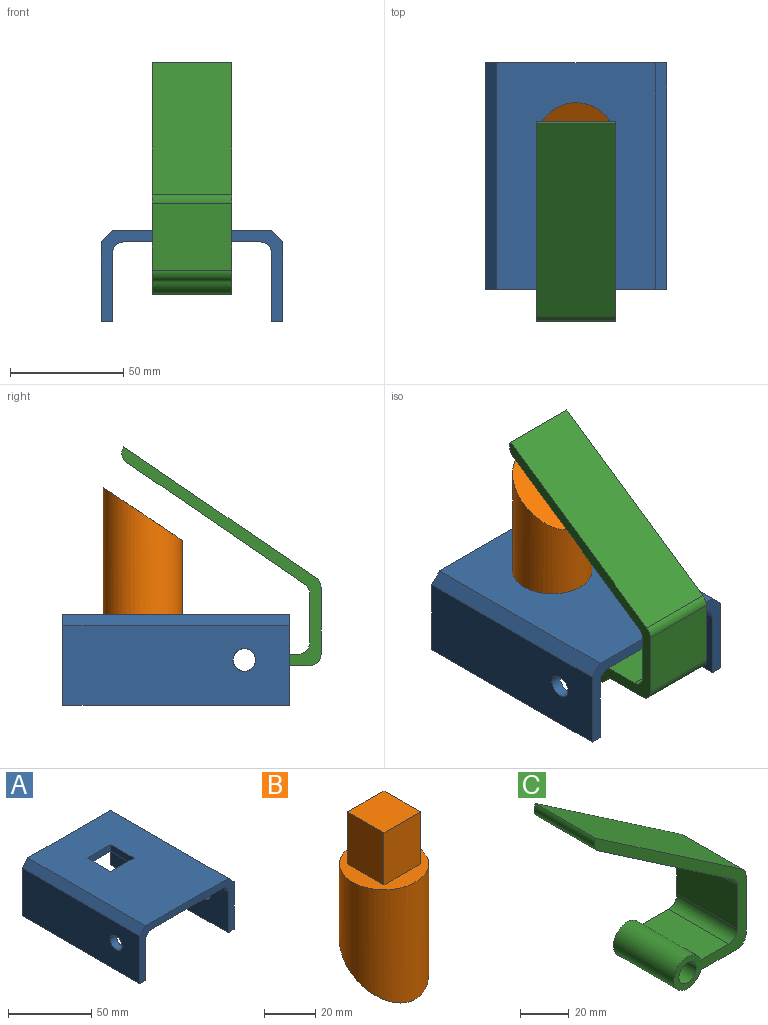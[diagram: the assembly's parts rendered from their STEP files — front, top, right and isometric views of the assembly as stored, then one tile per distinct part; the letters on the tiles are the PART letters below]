
ASSEMBLY  parts=3 mates=4
PART A: 20 faces, bbox 80x100x40 mm
  f0: plane 100x70mm, normal (0,0,1), area 6600mm2, adj f10,f11,f12,f13,f14,f15,f16,f17
  f1: plane 100x60mm, normal (0,0,-1), area 5600mm2, adj f2,f9,f10,f11,f14,f15,f16,f17
  f2: cylinder r=5mm len=100mm, axis (0,1,0), area 785.4mm2, adj f1,f3,f10,f11
  f3: plane 100x30mm, normal (-1,0,0), area 2921.5mm2, adj f2,f4,f10,f11,f19
  f4: plane 100x5mm, normal (0,0,-1), area 500mm2, adj f3,f5,f10,f11
  f5: plane 100x35mm, normal (1,0,0), area 3421.5mm2, adj f4,f10,f11,f13,f19
  f6: plane 100x35mm, normal (-1,0,0), area 3421.5mm2, adj f7,f10,f11,f12,f18
  f7: plane 100x5mm, normal (0,0,-1), area 500mm2, adj f6,f8,f10,f11
  f8: plane 100x30mm, normal (1,0,0), area 2921.5mm2, adj f7,f9,f10,f11,f18
  f9: cylinder r=5mm len=100mm, axis (0,1,0), area 785.4mm2, adj f1,f8,f10,f11
  f10: plane 80x40mm, normal (0,-1,0), area 735.7mm2, adj f0,f1,f2,f3,f4,f5,f6,f7
  f11: plane 80x40mm, normal (0,1,0), area 735.7mm2, adj f0,f1,f2,f3,f4,f5,f6,f7
  f12: plane 100x5mm, normal (-0.71,0,0.71), area 707.1mm2, adj f0,f6,f10,f11
  f13: plane 100x5mm, normal (0.71,0,0.71), area 707.1mm2, adj f0,f5,f10,f11
  f14: plane 20x5mm, normal (0,1,0), area 100mm2, adj f0,f1,f15,f17
  f15: plane 20x5mm, normal (-1,0,0), area 100mm2, adj f0,f1,f14,f16
  f16: plane 20x5mm, normal (0,-1,0), area 100mm2, adj f0,f1,f15,f17
  f17: plane 20x5mm, normal (1,0,0), area 100mm2, adj f0,f1,f14,f16
  f18: cylinder r=5mm len=10mm, axis (1,0,0), area 157.1mm2, adj f6,f8
  f19: cylinder r=5mm len=10mm, axis (1,0,0), area 157.1mm2, adj f3,f5
PART B: 8 faces, bbox 39.9x39.9x86.1 mm
  f0: cylinder r=17.5mm len=56.2mm, axis (0,0,1), area 4930.3mm2, adj f1,f7
  f1: plane 35x35mm, normal (0,0,1), area 562.1mm2, adj f0,f2,f3,f4,f5
  f2: plane 25x20mm, normal (1,0,0), area 500mm2, adj f1,f3,f5,f6
  f3: plane 25x20mm, normal (0,1,0), area 500mm2, adj f1,f2,f4,f6
  f4: plane 25x20mm, normal (-1,0,0), area 500mm2, adj f1,f3,f5,f6
  f5: plane 25x20mm, normal (0,-1,0), area 500mm2, adj f1,f2,f4,f6
  f6: plane 20x20mm, normal (0,0,1), area 400mm2, adj f2,f3,f4,f5
  f7: plane 39.92x39.92mm, normal (0,0.56,-0.83), area 1157.4mm2, adj f0
PART C: 15 faces, bbox 87.9x35x102.1 mm
  f0: plane 84.81x57.97mm, normal (0.56,0,0.83), area 3595.5mm2, adj f1,f12,f13,f14
  f1: cylinder r=5mm len=35mm, axis (0,-1,0), area 274.9mm2, adj f0,f2,f13,f14
  f2: plane 78.5x53.66mm, normal (-0.56,0,-0.83), area 3328.2mm2, adj f1,f3,f13,f14
  f3: cylinder r=5mm len=35mm, axis (0,-1,0), area 170mm2, adj f2,f4,f13,f14
  f4: plane 35x21.81mm, normal (-1,0,0), area 763.4mm2, adj f3,f5,f13,f14
  f5: cylinder r=5mm len=35mm, axis (0,-1,0), area 274.9mm2, adj f4,f6,f13,f14
  f6: plane 35x16.26mm, normal (0,0,1), area 569.1mm2, adj f5,f7,f13,f14
  f7: cylinder r=8mm len=35mm, axis (0,-1,0), area 1581.3mm2, adj f6,f8,f13,f14
  f8: plane 35x21.26mm, normal (0,0,-1), area 744.1mm2, adj f7,f9,f13,f14
  f9: cylinder r=5mm len=35mm, axis (0,-1,0), area 274.9mm2, adj f8,f10,f13,f14
  f10: plane 35x29.45mm, normal (1,0,0), area 1030.8mm2, adj f9,f12,f13,f14
  f11: cylinder r=5mm len=35mm, axis (0,-1,0), area 1099.6mm2, adj f13,f14
  f12: cylinder r=5mm len=35mm, axis (0,-1,0), area 170mm2, adj f0,f10,f13,f14
  f13: plane 102.05x87.86mm, normal (0,1,0), area 921.2mm2, adj f0,f1,f2,f3,f4,f5,f6,f7
  f14: plane 102.05x87.86mm, normal (0,-1,0), area 921.2mm2, adj f0,f1,f2,f3,f4,f5,f6,f7
PLACE A rot(axis=(1,0,0),0deg) t=(-101.49,13.62,40.58)mm
PLACE B rot(axis=(-1,0,0),180deg) t=(-101.49,28.45,110.58)mm
PLACE C rot(axis=(0,0,-1),90deg) t=(-101.49,-22.88,69.45)mm
MATE planar B.f5 <-> A.f16  axis (0,1,0) through (-111.49,38.45,35.58)mm
MATE planar B.f2 <-> A.f15  axis (1,0,0) through (-91.49,28.45,48.08)mm
MATE fastened C.f7 <-> A.f18  axis (-1,0,0) through (-101.49,-16.38,40.58)mm
MATE planar A.f0 <-> B.f1  axis (0,0,1) through (-101.49,12.72,60.58)mm
